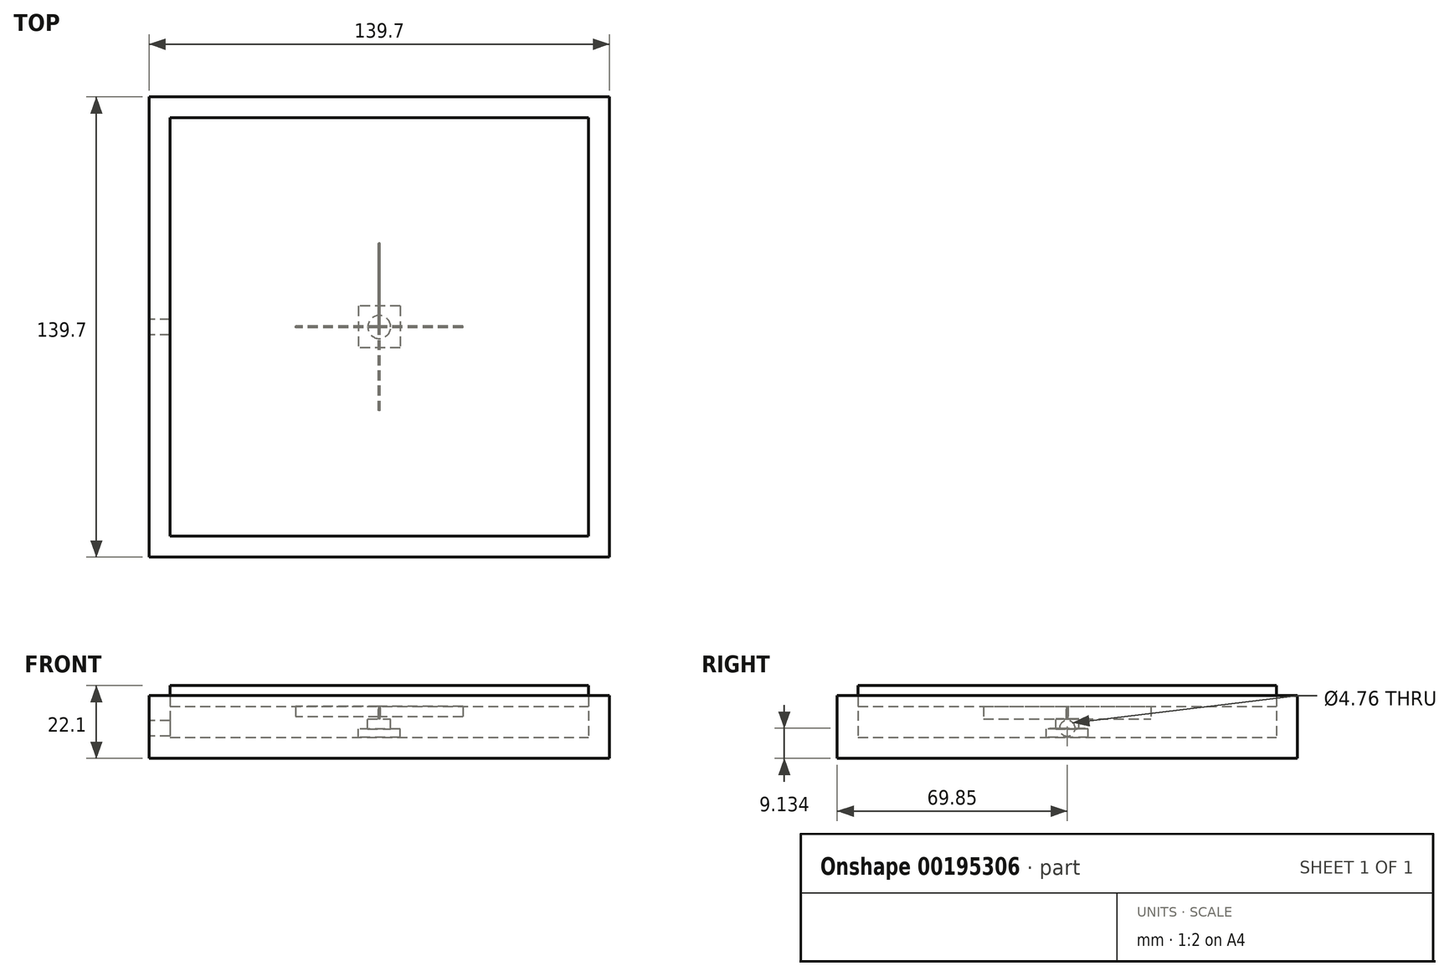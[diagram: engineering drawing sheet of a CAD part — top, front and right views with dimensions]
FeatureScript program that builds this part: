
annotation { "Feature Type Name" : "Feature", "Feature Type Description" : "" }
export const myFeature = defineFeature(function(context is Context, id is Id, definition is map)
    precondition{}
    {
        {
            var Q0;
            Q0=qCreatedBy(makeId("Top.planeOp"),FACE);
            var sketch = newSketch(context, id + "F0", { "sketchPlane" : qUnion([Q0])});
            skLineSegment(sketch, "E0.bottom", {"start": v(0, 0) * mm, "end": v(127, 0) * mm});
            skLineSegment(sketch, "E0.top", {"start": v(0, 127) * mm, "end": v(127, 127) * mm});
            skLineSegment(sketch, "E0.left", {"start": v(0, 0) * mm, "end": v(0, 127) * mm});
            skLineSegment(sketch, "E0.right", {"start": v(127, 0) * mm, "end": v(127, 127) * mm});
            skSolve(sketch);
        }
        {
            var Q0;
            Q0=makeQuery(id+"F0.imprint","IMPRINT",FACE,{"disambiguationData":[TD([[makeQuery(id+"F0.imprint","IMPRINT",EDGE,{"derivedFrom":sQuery(id+"F0.wireOp",EDGE,"E0.bottom")}),1.0]])]});
            extrude(context, id + "F1", {"entities" : qUnion([Q0]), "depth" : 6.35 * mm});
        }
        {
            var Q0;
            Q0=qCreatedBy(makeId("Right.planeOp"),FACE);
            cPlane(context, id + "F2", {"entities" : qUnion([Q0]), "cplaneType" : CPlaneType.OFFSET, "offset" : 63.5 * mm, "width" : 152.4 * mm, "height" : 152.4 * mm});
        }
        {
            var Q0;
            Q0=qCreatedBy(id+"F2.planeOp",FACE);
            var sketch = newSketch(context, id + "F3", { "sketchPlane" : qUnion([Q0])});
            skLineSegment(sketch, "E1.0", {"start": v(0, 0) * mm, "end": v(127, 0) * mm, "construction": true});
            skLineSegment(sketch, "E2", {"start": v(63.5, 0) * mm, "end": v(63.5, -53.96) * mm, "construction": true});
            skLineSegment(sketch, "E3.bottom", {"start": v(38.1, 0) * mm, "end": v(88.9, 0) * mm});
            skLineSegment(sketch, "E3.top", {"start": v(38.1, -3.81) * mm, "end": v(63.25, -3.81) * mm});
            skLineSegment(sketch, "E3.left", {"start": v(38.1, 0) * mm, "end": v(38.1, -3.81) * mm});
            skLineSegment(sketch, "E3.right", {"start": v(88.9, 0) * mm, "end": v(88.9, -3.8) * mm});
            skLineSegment(sketch, "E4.top", {"start": v(63.25, -0.63) * mm, "end": v(63.75, -0.63) * mm});
            skLineSegment(sketch, "E4.left", {"start": v(63.25, -3.81) * mm, "end": v(63.25, -0.63) * mm});
            skLineSegment(sketch, "E4.right", {"start": v(63.75, -3.81) * mm, "end": v(63.75, -0.63) * mm});
            skLineSegment(sketch, "E5.trimOffspring", {"start": v(63.75, -3.81) * mm, "end": v(88.9, -3.8) * mm});
            skSolve(sketch);
        }
        {
            var Q0;
            Q0=makeQuery(id+"F3.imprint","IMPRINT",FACE,{"disambiguationData":[TD([[makeQuery(id+"F3.imprint","IMPRINT",EDGE,{"derivedFrom":sQuery(id+"F3.wireOp",EDGE,"E3.bottom")}),-1.0]])]});
            extrude(context, id + "F4", {"entities" : qUnion([Q0]), "endBound" : BoundingType.SYMMETRIC, "depth" : 0.5 * mm});
        }
        {
            var Q0;
            Q0=qCreatedBy(makeId("Front.planeOp"),FACE);
            cPlane(context, id + "F5", {"entities" : qUnion([Q0]), "cplaneType" : CPlaneType.OFFSET, "offset" : 63.5 * mm, "oppositeDirection" : true, "width" : 152.4 * mm, "height" : 152.4 * mm});
        }
        {
            var Q0;
            Q0=qCreatedBy(id+"F5.planeOp",FACE);
            var sketch = newSketch(context, id + "F6", { "sketchPlane" : qUnion([Q0])});
            skLineSegment(sketch, "E6.0", {"start": v(0, 0) * mm, "end": v(63.25, 0) * mm, "construction": true});
            skLineSegment(sketch, "E7", {"start": v(63.5, 0) * mm, "end": v(63.5, -24.88) * mm, "construction": true});
            skLineSegment(sketch, "E8.bottom", {"start": v(88.9, 0) * mm, "end": v(63.75, 0) * mm});
            skLineSegment(sketch, "E8.top", {"start": v(88.9, -3.17) * mm, "end": v(38.1, -3.18) * mm});
            skLineSegment(sketch, "E8.left", {"start": v(88.9, 0) * mm, "end": v(88.9, -3.17) * mm});
            skLineSegment(sketch, "E8.right", {"start": v(38.1, 0) * mm, "end": v(38.1, -3.18) * mm});
            skLineSegment(sketch, "E9.top", {"start": v(63.75, -3.17) * mm, "end": v(63.25, -3.17) * mm});
            skLineSegment(sketch, "E9.left", {"start": v(63.75, 0) * mm, "end": v(63.75, -3.17) * mm});
            skLineSegment(sketch, "E9.right", {"start": v(63.25, 0) * mm, "end": v(63.25, -3.17) * mm});
            skLineSegment(sketch, "E10.trimOffspring", {"start": v(63.75, 0) * mm, "end": v(127, 0) * mm, "construction": true});
            skLineSegment(sketch, "E11.trimOffspring", {"start": v(63.25, 0) * mm, "end": v(38.1, 0) * mm});
            skSolve(sketch);
        }
        {
            var Q0;
            Q0 = qSketchRegion(id + "F6", true);
            extrude(context, id + "F7", {"entities" : qUnion([Q0]), "endBound" : BoundingType.SYMMETRIC, "depth" : 0.5 * mm});
        }
        {
            var Q0;
            Q0=makeQuery(id+"F4.opExtrude","SWEPT_FACE",FACE,{"disambiguationData":[OSD([sQuery(id+"F3.wireOp",EDGE,"E3.top")])]});
            var sketch = newSketch(context, id + "F8", { "sketchPlane" : qUnion([Q0])});
            skLineSegment(sketch, "E12.0", {"start": v(63.75, -38.1) * mm, "end": v(63.75, -60.02) * mm, "construction": true});
            skLineSegment(sketch, "E13.0", {"start": v(63.25, -38.1) * mm, "end": v(63.25, -60.02) * mm, "construction": true});
            skLineSegment(sketch, "E14.0", {"start": v(88.9, -63.25) * mm, "end": v(63.75, -63.25) * mm, "construction": true});
            skLineSegment(sketch, "E15.0", {"start": v(88.9, -63.75) * mm, "end": v(63.75, -63.75) * mm, "construction": true});
            skLineSegment(sketch, "E16", {"start": v(63.5, -63.25) * mm, "end": v(63.5, -64.17) * mm, "construction": true});
            skLineSegment(sketch, "E17", {"start": v(63.75, -63.75) * mm, "end": v(63.75, -63.25) * mm, "construction": true});
            skLineSegment(sketch, "E18", {"start": v(63.75, -63.5) * mm, "end": v(63.25, -63.5) * mm, "construction": true});
            skCircle(sketch, "E19", {"center": v(63.5, -63.5) * mm, "radius": 3.5 * mm});
            skPoint(sketch, "E20.orphan", {"position": v(63.25, -63.25) * mm});
            skLineSegment(sketch, "E21.trimOffspring", {"start": v(63.75, -63.25) * mm, "end": v(63.25, -63.25) * mm, "construction": true});
            skSolve(sketch);
        }
        {
            var Q0;
            {var subQ1=sQuery(id+"F3.wireOp",EDGE,"E3.top");var subQ6=makeQuery(id+"F4.opExtrude","SWEPT_EDGE",EDGE,{"disambiguationData":[OSD([subQ1,sQuery(id+"F3.wireOp",EDGE,"E4.left")])]});Q0=makeQuery(id+"F8.imprint","IMPRINT",FACE,{"disambiguationData":[TD([[makeQuery(id+"F8.imprint","IMPRINT",EDGE,{"derivedFrom":subQ6}),1.0]])]});}
            var Q1;
            {var subQ1=sQuery(id+"F3.wireOp",EDGE,"E3.top");var subQ6=makeQuery(id+"F4.opExtrude","SWEPT_EDGE",EDGE,{"disambiguationData":[OSD([subQ1,sQuery(id+"F3.wireOp",EDGE,"E4.left")])]});Q1=makeQuery(id+"F8.imprint","IMPRINT",FACE,{"disambiguationData":[TD([[makeQuery(id+"F8.imprint","IMPRINT",EDGE,{"derivedFrom":subQ6}),-1.0]])]});}
            extrude(context, id + "F9", {"entities" : qUnion([Q0, Q1]), "depth" : 3.05 * mm});
        }
        {
            var Q0;
            Q0=makeQuery(id+"F9.opExtrude","CAP_FACE",FACE,{"disambiguationData":[OSD([sQuery(id+"F8.wireOp",EDGE,"E19")])],"isStart":false});
            var sketch = newSketch(context, id + "F10", { "sketchPlane" : qUnion([Q0])});
            skCircle(sketch, "E22.0", {"center": v(63.5, -63.5) * mm, "radius": 3.5 * mm, "construction": true});
            skLineSegment(sketch, "E23", {"start": v(63.5, -63.5) * mm, "end": v(69.85, -63.5) * mm, "construction": true});
            skLineSegment(sketch, "E24", {"start": v(63.5, -63.5) * mm, "end": v(63.5, -72.16) * mm, "construction": true});
            skLineSegment(sketch, "E25.bottom", {"start": v(69.85, -69.85) * mm, "end": v(57.15, -69.85) * mm});
            skLineSegment(sketch, "E25.top", {"start": v(69.85, -57.15) * mm, "end": v(57.15, -57.15) * mm});
            skLineSegment(sketch, "E25.left", {"start": v(69.85, -69.85) * mm, "end": v(69.85, -57.15) * mm});
            skLineSegment(sketch, "E25.right", {"start": v(57.15, -69.85) * mm, "end": v(57.15, -57.15) * mm});
            skSolve(sketch);
        }
        {
            var Q0;
            Q0=makeQuery(id+"F10.imprint","IMPRINT",FACE,{"disambiguationData":[TD([[makeQuery(id+"F10.imprint","IMPRINT",EDGE,{"derivedFrom":sQuery(id+"F10.wireOp",EDGE,"E25.bottom")}),-1.0]])]});
            var Q1;
            Q1=makeQuery(id+"F10.imprint","IMPRINT",FACE,{"disambiguationData":[TD([[makeQuery(id+"F10.imprint","IMPRINT",EDGE,{"derivedFrom":makeQuery(id+"F9.opExtrude","CAP_EDGE",EDGE,{"disambiguationData":[OSD([sQuery(id+"F8.wireOp",EDGE,"E19")])],"isStart":false})}),1.0]])]});
            extrude(context, id + "F11", {"entities" : qUnion([Q0, Q1]), "operationType" : NewBodyOperationType.ADD, "depth" : 2.54 * mm});
        }
        {
            var Q0;
            Q0=makeQuery(id+"F11.opExtrude","CAP_FACE",FACE,{"disambiguationData":[OSD([sQuery(id+"F10.wireOp",EDGE,"E25.bottom"),sQuery(id+"F10.wireOp",EDGE,"E25.top"),sQuery(id+"F10.wireOp",EDGE,"E25.left"),sQuery(id+"F10.wireOp",EDGE,"E25.right")])],"isStart":false});
            var sketch = newSketch(context, id + "F12", { "sketchPlane" : qUnion([Q0])});
            skLineSegment(sketch, "E26.0", {"start": v(-6.35, 6.35) * mm, "end": v(133.35, 6.35) * mm});
            skLineSegment(sketch, "E26.1", {"start": v(-6.35, 6.35) * mm, "end": v(-6.35, -133.35) * mm});
            skLineSegment(sketch, "E26.2", {"start": v(-6.35, -133.35) * mm, "end": v(133.35, -133.35) * mm});
            skLineSegment(sketch, "E26.3", {"start": v(133.35, 6.35) * mm, "end": v(133.35, -133.35) * mm});
            skLineSegment(sketch, "E27.0", {"start": v(0, 0) * mm, "end": v(0, -127) * mm});
            skLineSegment(sketch, "E28.0", {"start": v(0, 0) * mm, "end": v(127, 0) * mm});
            skLineSegment(sketch, "E29.0", {"start": v(127, 0) * mm, "end": v(127, -127) * mm});
            skLineSegment(sketch, "E30.0", {"start": v(0, -127) * mm, "end": v(127, -127) * mm});
            skSolve(sketch);
        }
        {
            var Q0;
            Q0 = qSketchRegion(id + "F12", true);
            extrude(context, id + "F13", {"entities" : qUnion([Q0]), "oppositeDirection" : true, "depth" : 12.7 * mm});
        }
        {
            var Q0;
            Q0=makeQuery(id+"F11.opExtrude","CAP_FACE",FACE,{"disambiguationData":[OSD([sQuery(id+"F10.wireOp",EDGE,"E25.bottom"),sQuery(id+"F10.wireOp",EDGE,"E25.top"),sQuery(id+"F10.wireOp",EDGE,"E25.left"),sQuery(id+"F10.wireOp",EDGE,"E25.right")])],"isStart":false});
            var sketch = newSketch(context, id + "F14", { "sketchPlane" : qUnion([Q0])});
            skLineSegment(sketch, "E31.0", {"start": v(-6.35, 6.35) * mm, "end": v(-6.35, -133.35) * mm});
            skLineSegment(sketch, "E32.0", {"start": v(-6.35, 6.35) * mm, "end": v(133.35, 6.35) * mm});
            skLineSegment(sketch, "E33.0", {"start": v(133.35, 6.35) * mm, "end": v(133.35, -133.35) * mm});
            skLineSegment(sketch, "E34.0", {"start": v(-6.35, -133.35) * mm, "end": v(133.35, -133.35) * mm});
            skSolve(sketch);
        }
        {
            var Q0;
            Q0=makeQuery(id+"F14.imprint","IMPRINT",FACE,{"disambiguationData":[TD([[makeQuery(id+"F14.imprint","IMPRINT",EDGE,{"derivedFrom":makeQuery(id+"F11.opExtrude","CAP_EDGE",EDGE,{"disambiguationData":[OSD([sQuery(id+"F10.wireOp",EDGE,"E25.bottom")])],"isStart":false})}),-1.0]])]});
            var sketch = newSketch(context, id + "F15", { "sketchPlane" : qUnion([Q0])});
            skLineSegment(sketch, "E35.0", {"start": v(-6.35, 6.35) * mm, "end": v(133.35, 6.35) * mm});
            skLineSegment(sketch, "E36.0", {"start": v(-6.35, 6.35) * mm, "end": v(-6.35, -133.35) * mm});
            skLineSegment(sketch, "E37.0", {"start": v(133.35, 6.35) * mm, "end": v(133.35, -133.35) * mm});
            skLineSegment(sketch, "E38.0", {"start": v(-6.35, -133.35) * mm, "end": v(133.35, -133.35) * mm});
            skSolve(sketch);
        }
        {
            var Q0;
            Q0 = qSketchRegion(id + "F15", true);
            extrude(context, id + "F16", {"entities" : qUnion([Q0]), "operationType" : NewBodyOperationType.ADD, "depth" : 6.35 * mm});
        }
        {
            var Q0;
            Q0=qCreatedBy(id+"F2.planeOp",FACE);
            var sketch = newSketch(context, id + "F17", { "sketchPlane" : qUnion([Q0])});
            skCircle(sketch, "E39", {"center": v(63.5, -6.62) * mm, "radius": 2.38 * mm});
            skLineSegment(sketch, "E40.0", {"start": v(-6.35, -15.75) * mm, "end": v(133.35, -15.75) * mm, "construction": true});
            skLineSegment(sketch, "E41", {"start": v(63.5, -15.75) * mm, "end": v(63.5, 4.04) * mm, "construction": true});
            skSolve(sketch);
        }
        {
            var Q0;
            Q0=makeQuery(id+"F16.boolean.opBoolean","MERGE",FACE,{"derivedFrom":[makeQuery(id+"F13.opExtrude","SWEPT_FACE",FACE,{"disambiguationData":[OSD([sQuery(id+"F12.wireOp",EDGE,"E26.1")])]}),makeQuery(id+"F16.opExtrude","SWEPT_FACE",FACE,{"disambiguationData":[OSD([sQuery(id+"F15.wireOp",EDGE,"E36.0")])]})]});
            var sketch = newSketch(context, id + "F18", { "sketchPlane" : qUnion([Q0])});
            skCircle(sketch, "E42.0", {"center": v(-63.5, -6.62) * mm, "radius": 2.38 * mm});
            skSolve(sketch);
        }
        {
            var Q0;
            Q0 = qSketchRegion(id + "F18", true);
            extrude(context, id + "F19", {"entities" : qUnion([Q0]), "operationType" : NewBodyOperationType.REMOVE, "oppositeDirection" : true, "depth" : 25.4 * mm});
        }
    });
